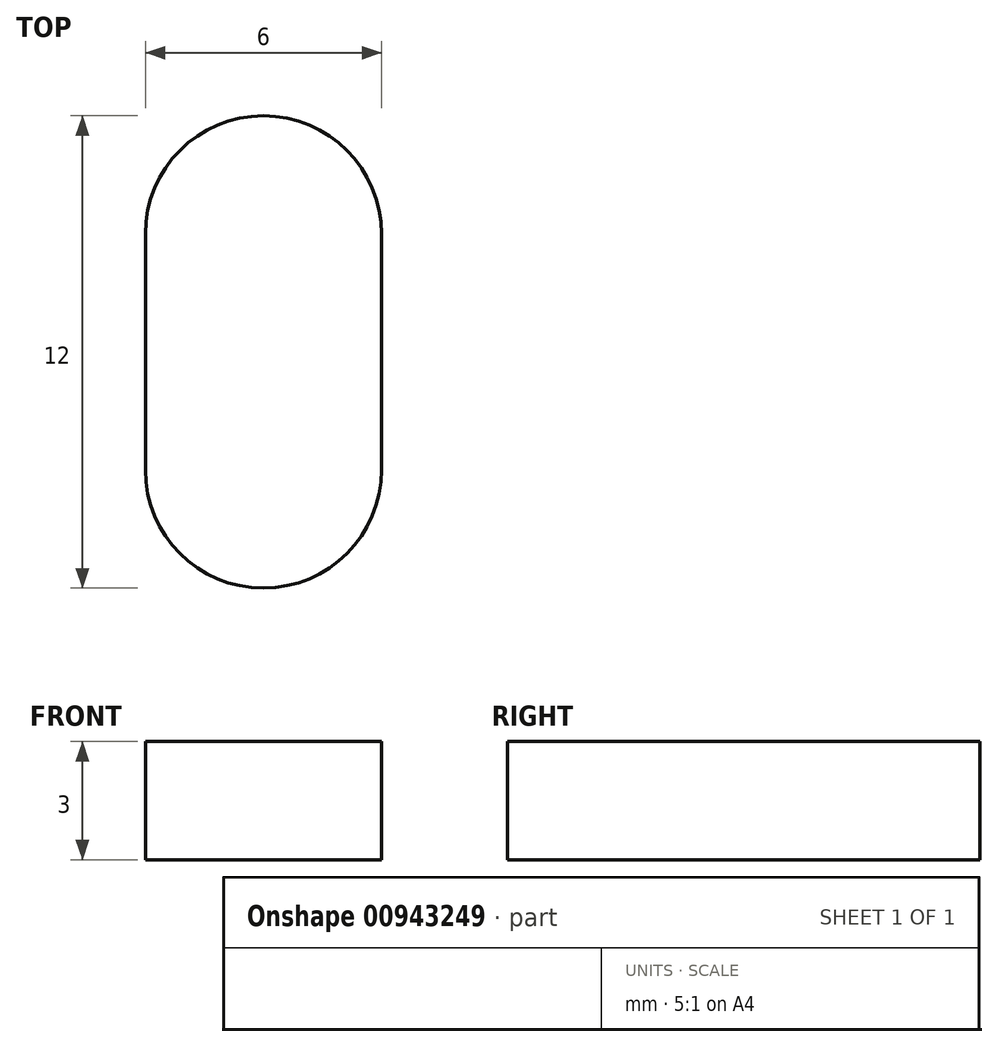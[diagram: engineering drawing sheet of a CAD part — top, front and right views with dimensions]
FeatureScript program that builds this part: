
annotation { "Feature Type Name" : "Feature", "Feature Type Description" : "" }
export const myFeature = defineFeature(function(context is Context, id is Id, definition is map)
    precondition{}
    {
        {
            var Q0;
            Q0=qCreatedBy(makeId("Top.planeOp"),FACE);
            var sketch = newSketch(context, id + "F0", { "sketchPlane" : qUnion([Q0])});
            skLineSegment(sketch, "E0", {"start": v(0, -3) * mm, "end": v(0, 3) * mm});
            skArc(sketch, "E1.0.startCap", {"start": v(3, -3) * mm, "mid": v(0, -6) * mm, "end": v(-3, -3) * mm});
            skArc(sketch, "E1.0.endCap", {"start": v(-3, 3) * mm, "mid": v(0, 6) * mm, "end": v(3, 3) * mm});
            skLineSegment(sketch, "E1.0.left", {"start": v(-3, -3) * mm, "end": v(-3, 3) * mm});
            skLineSegment(sketch, "E1.0.right", {"start": v(3, -3) * mm, "end": v(3, 3) * mm});
            skSolve(sketch);
        }
        {
            var Q0;
            Q0=qSketchRegion(id+"F0",true);
            extrude(context, id + "F1", {"entities" : qUnion([Q0]), "depth" : 3 * mm, "offsetDistance" : 25 * mm});
        }
    });
